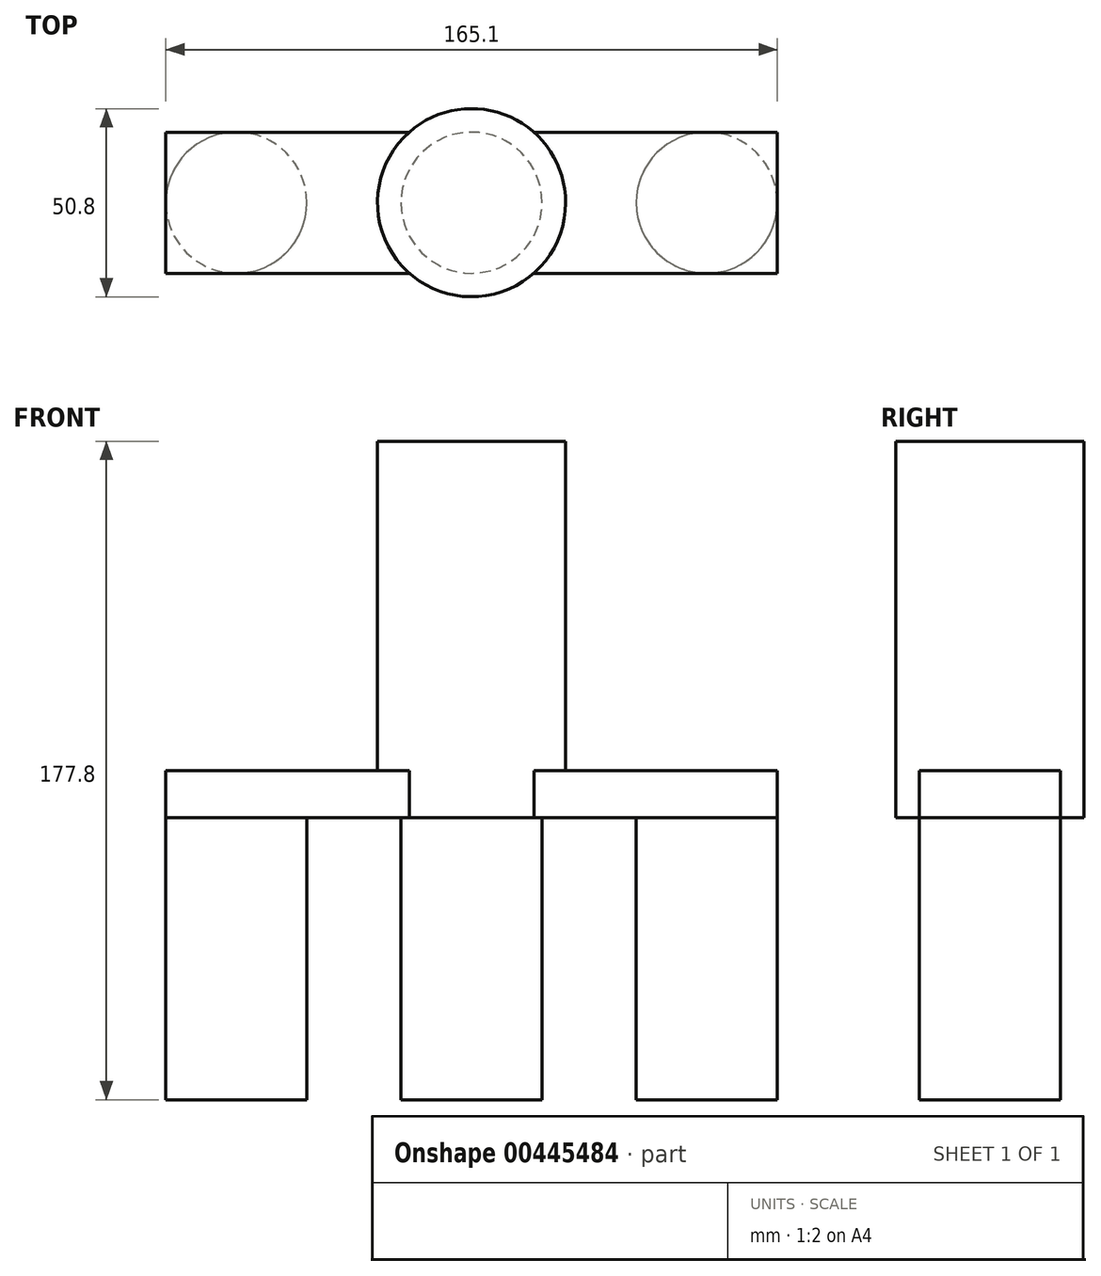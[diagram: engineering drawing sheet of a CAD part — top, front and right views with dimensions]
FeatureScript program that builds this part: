
annotation { "Feature Type Name" : "Feature", "Feature Type Description" : "" }
export const myFeature = defineFeature(function(context is Context, id is Id, definition is map)
    precondition{}
    {
        {
            var Q0;
            Q0=qCreatedBy(makeId("Top.planeOp"),FACE);
            var sketch = newSketch(context, id + "F0", { "sketchPlane" : qUnion([Q0])});
            skCircle(sketch, "E0", {"center": v(0, 0) * mm, "radius": 25.4 * mm});
            skPoint(sketch, "E1", {"position": v(63.5, 0) * mm});
            skPoint(sketch, "E2", {"position": v(-63.5, 0) * mm});
            skCircle(sketch, "E3", {"center": v(-63.5, 0) * mm, "radius": 19.05 * mm});
            skCircle(sketch, "E4", {"center": v(63.5, 0) * mm, "radius": 19.05 * mm});
            skLineSegment(sketch, "E5.bottom", {"start": v(82.55, 19.05) * mm, "end": v(-82.55, 19.05) * mm});
            skLineSegment(sketch, "E5.top", {"start": v(82.55, -19.05) * mm, "end": v(-82.55, -19.05) * mm});
            skLineSegment(sketch, "E5.left", {"start": v(82.55, 19.05) * mm, "end": v(82.55, -19.05) * mm});
            skLineSegment(sketch, "E5.right", {"start": v(-82.55, 19.05) * mm, "end": v(-82.55, -19.05) * mm});
            skCircle(sketch, "E6", {"center": v(0, 0) * mm, "radius": 19.05 * mm});
            skSolve(sketch);
        }
        {
            var Q0;
            {var subQ0=sQuery(id+"F0.wireOp",EDGE,"E5.bottom");var subQ1=sQuery(id+"F0.wireOp",EDGE,"E0");var subQ2=makeQuery(id+"F0.imprint","INTERSECT",VERTEX,{"disambiguationData":[OD(0.0)],"derivedFrom":[subQ1,subQ0]});Q0=makeQuery(id+"F0.imprint","IMPRINT",FACE,{"disambiguationData":[TD([[makeQuery(id+"F0.imprint","IMPRINT",EDGE,{"disambiguationData":[TD([[subQ2,-1.0]])],"derivedFrom":subQ1}),-1.0]])]});}
            var Q1;
            {var subQ0=sQuery(id+"F0.wireOp",EDGE,"E5.right");var subQ1=sQuery(id+"F0.wireOp",EDGE,"E3");var subQ2=makeQuery(id+"F0.imprint","INTERSECT",VERTEX,{"derivedFrom":[subQ1,subQ0]});Q1=makeQuery(id+"F0.imprint","IMPRINT",FACE,{"disambiguationData":[TD([[makeQuery(id+"F0.imprint","IMPRINT",EDGE,{"disambiguationData":[TD([[subQ2,1.0]])],"derivedFrom":subQ1}),-1.0]])]});}
            var Q2;
            {var subQ0=sQuery(id+"F0.wireOp",EDGE,"E5.right");var subQ1=sQuery(id+"F0.wireOp",EDGE,"E3");var subQ2=makeQuery(id+"F0.imprint","INTERSECT",VERTEX,{"derivedFrom":[subQ1,subQ0]});Q2=makeQuery(id+"F0.imprint","IMPRINT",FACE,{"disambiguationData":[TD([[makeQuery(id+"F0.imprint","IMPRINT",EDGE,{"disambiguationData":[TD([[subQ2,-1.0]])],"derivedFrom":subQ1}),-1.0]])]});}
            var Q3;
            {var subQ0=sQuery(id+"F0.wireOp",EDGE,"E5.bottom");var subQ1=sQuery(id+"F0.wireOp",EDGE,"E4");var subQ2=makeQuery(id+"F0.imprint","INTERSECT",VERTEX,{"derivedFrom":[subQ1,subQ0]});Q3=makeQuery(id+"F0.imprint","IMPRINT",FACE,{"disambiguationData":[TD([[makeQuery(id+"F0.imprint","IMPRINT",EDGE,{"disambiguationData":[TD([[subQ2,1.0]])],"derivedFrom":subQ1}),-1.0]])]});}
            var Q4;
            {var subQ0=sQuery(id+"F0.wireOp",EDGE,"E5.left");var subQ1=sQuery(id+"F0.wireOp",EDGE,"E4");var subQ2=makeQuery(id+"F0.imprint","INTERSECT",VERTEX,{"derivedFrom":[subQ1,subQ0]});Q4=makeQuery(id+"F0.imprint","IMPRINT",FACE,{"disambiguationData":[TD([[makeQuery(id+"F0.imprint","IMPRINT",EDGE,{"disambiguationData":[TD([[subQ2,1.0]])],"derivedFrom":subQ1}),-1.0]])]});}
            var Q5;
            {var subQ0=sQuery(id+"F0.wireOp",EDGE,"E5.bottom");var subQ1=sQuery(id+"F0.wireOp",EDGE,"E0");var subQ2=makeQuery(id+"F0.imprint","INTERSECT",VERTEX,{"disambiguationData":[OD(1.0)],"derivedFrom":[subQ1,subQ0]});Q5=makeQuery(id+"F0.imprint","IMPRINT",FACE,{"disambiguationData":[TD([[makeQuery(id+"F0.imprint","IMPRINT",EDGE,{"disambiguationData":[TD([[subQ2,1.0]])],"derivedFrom":subQ1}),-1.0]])]});}
            var Q6;
            {var subQ0=sQuery(id+"F0.wireOp",EDGE,"E4");var subQ1=makeQuery(id+"F0.imprint","INTERSECT",VERTEX,{"derivedFrom":[subQ0,sQuery(id+"F0.wireOp",EDGE,"E5.bottom")]});Q6=makeQuery(id+"F0.imprint","IMPRINT",FACE,{"disambiguationData":[TD([[makeQuery(id+"F0.imprint","IMPRINT",EDGE,{"disambiguationData":[TD([[subQ1,1.0]])],"derivedFrom":subQ0}),1.0]])]});}
            var Q7;
            {var subQ0=sQuery(id+"F0.wireOp",EDGE,"E6");var subQ1=makeQuery(id+"F0.imprint","INTERSECT",VERTEX,{"derivedFrom":[sQuery(id+"F0.wireOp",EDGE,"E5.bottom"),subQ0]});Q7=makeQuery(id+"F0.imprint","IMPRINT",FACE,{"disambiguationData":[TD([[makeQuery(id+"F0.imprint","IMPRINT",EDGE,{"disambiguationData":[TD([[subQ1,-1.0]])],"derivedFrom":subQ0}),1.0]])]});}
            var Q8;
            {var subQ0=sQuery(id+"F0.wireOp",EDGE,"E5.bottom");var subQ1=sQuery(id+"F0.wireOp",EDGE,"E0");var subQ2=makeQuery(id+"F0.imprint","INTERSECT",VERTEX,{"disambiguationData":[OD(1.0)],"derivedFrom":[subQ1,subQ0]});Q8=makeQuery(id+"F0.imprint","IMPRINT",FACE,{"disambiguationData":[TD([[makeQuery(id+"F0.imprint","IMPRINT",EDGE,{"disambiguationData":[TD([[subQ2,1.0]])],"derivedFrom":subQ1}),1.0]])]});}
            var Q9;
            {var subQ0=sQuery(id+"F0.wireOp",EDGE,"E5.bottom");var subQ1=sQuery(id+"F0.wireOp",EDGE,"E0");var subQ2=makeQuery(id+"F0.imprint","INTERSECT",VERTEX,{"disambiguationData":[OD(0.0)],"derivedFrom":[subQ1,subQ0]});Q9=makeQuery(id+"F0.imprint","IMPRINT",FACE,{"disambiguationData":[TD([[makeQuery(id+"F0.imprint","IMPRINT",EDGE,{"disambiguationData":[TD([[subQ2,-1.0]])],"derivedFrom":subQ1}),1.0]])]});}
            var Q10;
            {var subQ0=sQuery(id+"F0.wireOp",EDGE,"E3");var subQ1=makeQuery(id+"F0.imprint","INTERSECT",VERTEX,{"derivedFrom":[subQ0,sQuery(id+"F0.wireOp",EDGE,"E5.right")]});Q10=makeQuery(id+"F0.imprint","IMPRINT",FACE,{"disambiguationData":[TD([[makeQuery(id+"F0.imprint","IMPRINT",EDGE,{"disambiguationData":[TD([[subQ1,1.0]])],"derivedFrom":subQ0}),1.0]])]});}
            extrude(context, id + "F1", {"entities" : qUnion([Q0, Q1, Q2, Q3, Q4, Q5, Q6, Q7, Q8, Q9, Q10]), "depth" : 12.7 * mm});
        }
        {
            var Q0;
            {var subQ0=sQuery(id+"F0.wireOp",EDGE,"E5.bottom");var subQ1=sQuery(id+"F0.wireOp",EDGE,"E0");var subQ2=makeQuery(id+"F0.imprint","INTERSECT",VERTEX,{"disambiguationData":[OD(0.0)],"derivedFrom":[subQ1,subQ0]});Q0=makeQuery(id+"F0.imprint","IMPRINT",FACE,{"disambiguationData":[TD([[makeQuery(id+"F0.imprint","IMPRINT",EDGE,{"disambiguationData":[TD([[subQ2,1.0]])],"derivedFrom":subQ1}),1.0]])]});}
            var Q1;
            {var subQ0=sQuery(id+"F0.wireOp",EDGE,"E5.bottom");var subQ1=sQuery(id+"F0.wireOp",EDGE,"E0");var subQ2=makeQuery(id+"F0.imprint","INTERSECT",VERTEX,{"disambiguationData":[OD(1.0)],"derivedFrom":[subQ1,subQ0]});Q1=makeQuery(id+"F0.imprint","IMPRINT",FACE,{"disambiguationData":[TD([[makeQuery(id+"F0.imprint","IMPRINT",EDGE,{"disambiguationData":[TD([[subQ2,1.0]])],"derivedFrom":subQ1}),1.0]])]});}
            var Q2;
            {var subQ0=sQuery(id+"F0.wireOp",EDGE,"E6");var subQ1=makeQuery(id+"F0.imprint","INTERSECT",VERTEX,{"derivedFrom":[sQuery(id+"F0.wireOp",EDGE,"E5.bottom"),subQ0]});Q2=makeQuery(id+"F0.imprint","IMPRINT",FACE,{"disambiguationData":[TD([[makeQuery(id+"F0.imprint","IMPRINT",EDGE,{"disambiguationData":[TD([[subQ1,-1.0]])],"derivedFrom":subQ0}),1.0]])]});}
            var Q3;
            {var subQ0=sQuery(id+"F0.wireOp",EDGE,"E5.bottom");var subQ1=sQuery(id+"F0.wireOp",EDGE,"E0");var subQ2=makeQuery(id+"F0.imprint","INTERSECT",VERTEX,{"disambiguationData":[OD(0.0)],"derivedFrom":[subQ1,subQ0]});Q3=makeQuery(id+"F0.imprint","IMPRINT",FACE,{"disambiguationData":[TD([[makeQuery(id+"F0.imprint","IMPRINT",EDGE,{"disambiguationData":[TD([[subQ2,-1.0]])],"derivedFrom":subQ1}),1.0]])]});}
            var Q4;
            {var subQ0=sQuery(id+"F0.wireOp",EDGE,"E5.top");var subQ1=sQuery(id+"F0.wireOp",EDGE,"E0");var subQ2=makeQuery(id+"F0.imprint","INTERSECT",VERTEX,{"disambiguationData":[OD(0.0)],"derivedFrom":[subQ1,subQ0]});Q4=makeQuery(id+"F0.imprint","IMPRINT",FACE,{"disambiguationData":[TD([[makeQuery(id+"F0.imprint","IMPRINT",EDGE,{"disambiguationData":[TD([[subQ2,-1.0]])],"derivedFrom":subQ1}),1.0]])]});}
            extrude(context, id + "F2", {"entities" : qUnion([Q0, Q1, Q2, Q3, Q4]), "operationType" : NewBodyOperationType.ADD, "depth" : 101.6 * mm});
        }
        {
            var Q0;
            {var subQ0=sQuery(id+"F0.wireOp",EDGE,"E4");var subQ1=makeQuery(id+"F0.imprint","INTERSECT",VERTEX,{"derivedFrom":[subQ0,sQuery(id+"F0.wireOp",EDGE,"E5.bottom")]});Q0=makeQuery(id+"F0.imprint","IMPRINT",FACE,{"disambiguationData":[TD([[makeQuery(id+"F0.imprint","IMPRINT",EDGE,{"disambiguationData":[TD([[subQ1,1.0]])],"derivedFrom":subQ0}),1.0]])]});}
            var Q1;
            {var subQ0=sQuery(id+"F0.wireOp",EDGE,"E6");var subQ1=makeQuery(id+"F0.imprint","INTERSECT",VERTEX,{"derivedFrom":[sQuery(id+"F0.wireOp",EDGE,"E5.bottom"),subQ0]});Q1=makeQuery(id+"F0.imprint","IMPRINT",FACE,{"disambiguationData":[TD([[makeQuery(id+"F0.imprint","IMPRINT",EDGE,{"disambiguationData":[TD([[subQ1,-1.0]])],"derivedFrom":subQ0}),1.0]])]});}
            var Q2;
            {var subQ0=sQuery(id+"F0.wireOp",EDGE,"E3");var subQ1=makeQuery(id+"F0.imprint","INTERSECT",VERTEX,{"derivedFrom":[subQ0,sQuery(id+"F0.wireOp",EDGE,"E5.right")]});Q2=makeQuery(id+"F0.imprint","IMPRINT",FACE,{"disambiguationData":[TD([[makeQuery(id+"F0.imprint","IMPRINT",EDGE,{"disambiguationData":[TD([[subQ1,1.0]])],"derivedFrom":subQ0}),1.0]])]});}
            extrude(context, id + "F3", {"entities" : qUnion([Q0, Q1, Q2]), "operationType" : NewBodyOperationType.ADD, "oppositeDirection" : true, "depth" : 76.2 * mm});
        }
    });
